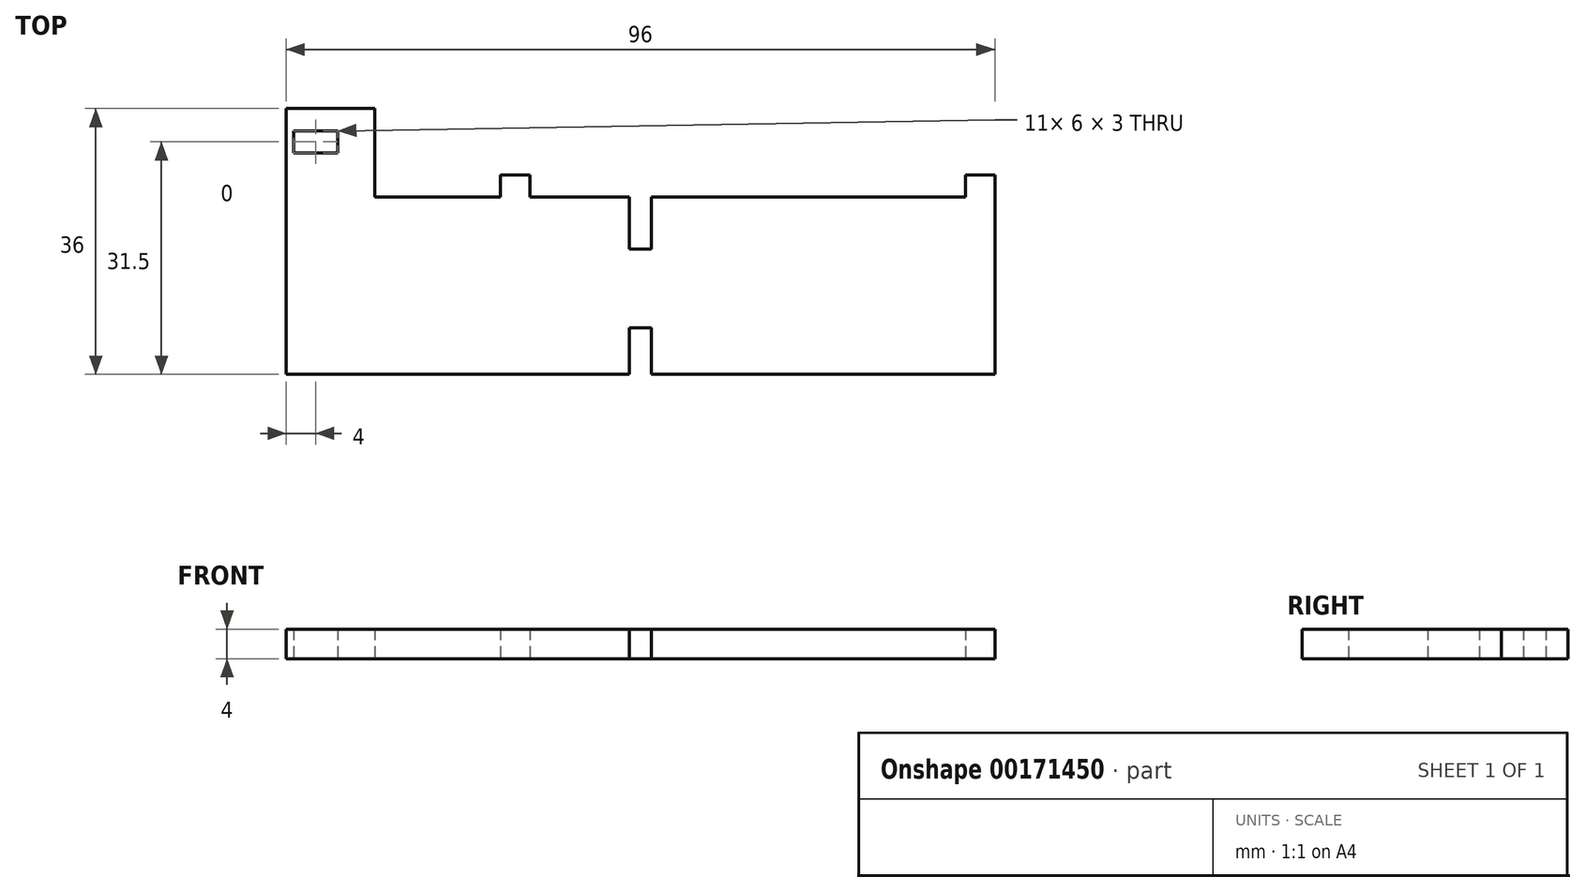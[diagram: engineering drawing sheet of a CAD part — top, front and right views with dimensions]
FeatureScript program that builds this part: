
annotation { "Feature Type Name" : "Feature", "Feature Type Description" : "" }
export const myFeature = defineFeature(function(context is Context, id is Id, definition is map)
    precondition{}
    {
        {
            var Q0;
            Q0=qCreatedBy(makeId("Top.planeOp"),FACE);
            var sketch = newSketch(context, id + "F0", { "sketchPlane" : qUnion([Q0])});
            skLineSegment(sketch, "E0.bottom", {"start": v(48, -12) * mm, "end": v(-48, -12) * mm});
            skLineSegment(sketch, "E0.left", {"start": v(48, -12) * mm, "end": v(48, 12) * mm});
            skLineSegment(sketch, "E0.right", {"start": v(-48, -12) * mm, "end": v(-48, 12) * mm});
            skPoint(sketch, "E0.middle", {"position": v(0, 0) * mm});
            skLineSegment(sketch, "E1.bottom", {"start": v(48, 12) * mm, "end": v(44, 12) * mm});
            skLineSegment(sketch, "E1.top", {"start": v(48, 15) * mm, "end": v(44, 15) * mm});
            skLineSegment(sketch, "E1.left", {"start": v(48, 12) * mm, "end": v(48, 15) * mm});
            skLineSegment(sketch, "E1.right", {"start": v(44, 12) * mm, "end": v(44, 15) * mm});
            skLineSegment(sketch, "E2.bottom", {"start": v(-48, 12) * mm, "end": v(-36, 12) * mm});
            skLineSegment(sketch, "E2.top", {"start": v(-48, 24) * mm, "end": v(-36, 24) * mm});
            skLineSegment(sketch, "E2.left", {"start": v(-48, 12) * mm, "end": v(-48, 24) * mm});
            skLineSegment(sketch, "E2.right", {"start": v(-36, 12) * mm, "end": v(-36, 24) * mm});
            skLineSegment(sketch, "E3.bottom", {"start": v(-36, 12) * mm, "end": v(-36, 12) * mm});
            skLineSegment(sketch, "E3.top", {"start": v(-36, 12) * mm, "end": v(-36, 12) * mm});
            skLineSegment(sketch, "E3.left", {"start": v(-36, 12) * mm, "end": v(-36, 12) * mm});
            skLineSegment(sketch, "E3.right", {"start": v(-36, 12) * mm, "end": v(-36, 12) * mm});
            skPoint(sketch, "E3.middle", {"position": v(-36, 12) * mm});
            skLineSegment(sketch, "E4.bottom", {"start": v(-15, 12) * mm, "end": v(-19, 12) * mm});
            skLineSegment(sketch, "E4.top", {"start": v(-15, 15) * mm, "end": v(-19, 15) * mm});
            skLineSegment(sketch, "E4.left", {"start": v(-15, 12) * mm, "end": v(-15, 15) * mm});
            skLineSegment(sketch, "E4.right", {"start": v(-19, 12) * mm, "end": v(-19, 15) * mm});
            skPoint(sketch, "E4.middle", {"position": v(-17, 13.5) * mm});
            skLineSegment(sketch, "E5.bottom", {"start": v(-1.5, -5) * mm, "end": v(1.5, -5) * mm});
            skLineSegment(sketch, "E5.top", {"start": v(-1.5, 5) * mm, "end": v(1.5, 5) * mm});
            skLineSegment(sketch, "E5.left", {"start": v(-1.5, -5) * mm, "end": v(-1.5, 5) * mm});
            skLineSegment(sketch, "E5.right", {"start": v(1.5, -5) * mm, "end": v(1.5, 5) * mm});
            skLineSegment(sketch, "E6.left", {"start": v(4.5, 12) * mm, "end": v(4.5, 12) * mm});
            skLineSegment(sketch, "E6.right", {"start": v(-4.5, 12) * mm, "end": v(-4.5, 12) * mm});
            skPoint(sketch, "E6.middle", {"position": v(0, 12) * mm});
            skLineSegment(sketch, "E7", {"start": v(-36, 12) * mm, "end": v(44, 12) * mm});
            skLineSegment(sketch, "E8.bottom", {"start": v(1.5, 5) * mm, "end": v(-1.5, 5) * mm});
            skLineSegment(sketch, "E8.top", {"start": v(1.5, 12.87) * mm, "end": v(-1.5, 12.87) * mm});
            skLineSegment(sketch, "E8.left", {"start": v(1.5, 5) * mm, "end": v(1.5, 12.87) * mm});
            skLineSegment(sketch, "E8.right", {"start": v(-1.5, 5) * mm, "end": v(-1.5, 12.87) * mm});
            skPoint(sketch, "E8.middle", {"position": v(0, 8.94) * mm});
            skLineSegment(sketch, "E9.left", {"start": v(-36, 18) * mm, "end": v(-36, 18) * mm});
            skLineSegment(sketch, "E9.right", {"start": v(-48, 18) * mm, "end": v(-48, 18) * mm});
            skPoint(sketch, "E9.middle.positionSnap0", {"position": v(-48, 18) * mm});
            skPoint(sketch, "E9.middle.positionSnap1", {"position": v(-42, 12) * mm});
            skPoint(sketch, "E9.centerSnap0", {"position": v(-48, 18) * mm});
            skPoint(sketch, "E9.centerSnap1", {"position": v(-42, 12) * mm});
            skLineSegment(sketch, "E10", {"start": v(-47, 18) * mm, "end": v(-41, 18) * mm});
            skLineSegment(sketch, "E11", {"start": v(-47, 18) * mm, "end": v(-47, 21) * mm});
            skLineSegment(sketch, "E12", {"start": v(-47, 21) * mm, "end": v(-41, 21) * mm});
            skLineSegment(sketch, "E13", {"start": v(-41, 21) * mm, "end": v(-41, 18) * mm});
            skLineSegment(sketch, "E14.bottom", {"start": v(1.5, -12) * mm, "end": v(-1.5, -12) * mm});
            skLineSegment(sketch, "E14.top", {"start": v(1.5, -5.69) * mm, "end": v(-1.5, -5.69) * mm});
            skLineSegment(sketch, "E14.left", {"start": v(1.5, -12) * mm, "end": v(1.5, -5.69) * mm});
            skLineSegment(sketch, "E14.right", {"start": v(-1.5, -12) * mm, "end": v(-1.5, -5.69) * mm});
            skPoint(sketch, "E14.middle", {"position": v(0, -8.84) * mm});
            skSolve(sketch);
        }
        {
            var Q0;
            Q0=makeQuery(id+"F0.imprint","IMPRINT",FACE,{"disambiguationData":[TD([[makeQuery(id+"F0.imprint","IMPRINT",EDGE,{"derivedFrom":sQuery(id+"F0.wireOp",EDGE,"E1.bottom")}),-1.0]])]});
            var Q1;
            Q1=makeQuery(id+"F0.imprint","IMPRINT",FACE,{"disambiguationData":[TD([[makeQuery(id+"F0.imprint","IMPRINT",EDGE,{"derivedFrom":sQuery(id+"F0.wireOp",EDGE,"E4.top")}),1.0]])]});
            var Q2;
            Q2=makeQuery(id+"F0.imprint","IMPRINT",FACE,{"disambiguationData":[TD([[makeQuery(id+"F0.imprint","IMPRINT",EDGE,{"derivedFrom":sQuery(id+"F0.wireOp",EDGE,"E2.bottom")}),1.0]])]});
            var Q3;
            {var subQ11=sQuery(id+"F0.wireOp",EDGE,"E0.left");Q3=makeQuery(id+"F0.imprint","IMPRINT",FACE,{"disambiguationData":[TD([[makeQuery(id+"F0.imprint","IMPRINT",EDGE,{"derivedFrom":subQ11}),1.0]])]});}
            var Q4;
            Q4=makeQuery(id+"F0.imprint","IMPRINT",FACE,{"disambiguationData":[TD([[makeQuery(id+"F0.imprint","IMPRINT",EDGE,{"derivedFrom":sQuery(id+"F0.wireOp",EDGE,"E5.bottom")}),1.0]])]});
            extrude(context, id + "F1", {"entities" : qUnion([Q0, Q1, Q2, Q3, Q4]), "depth" : 4 * mm});
        }
    });
